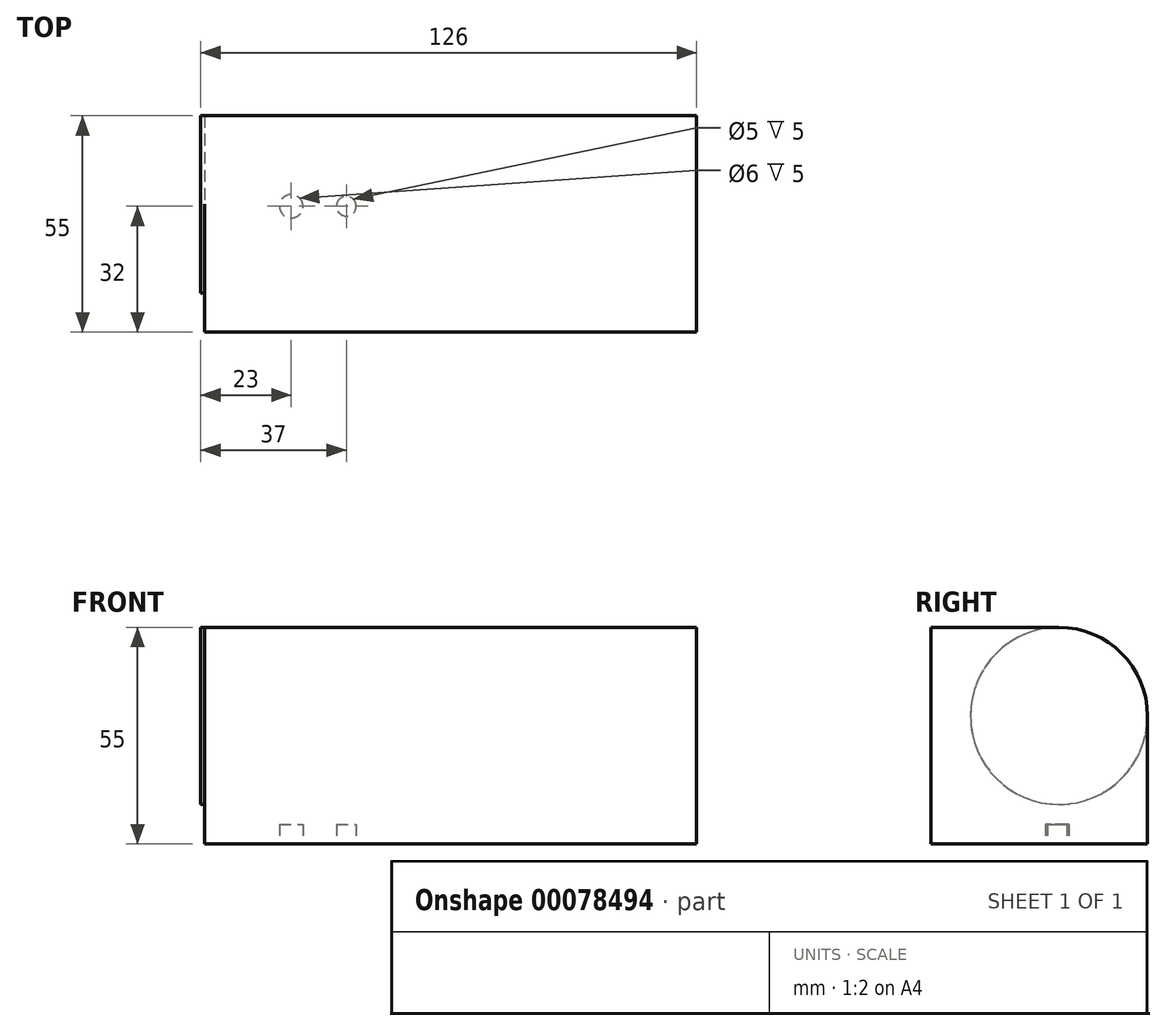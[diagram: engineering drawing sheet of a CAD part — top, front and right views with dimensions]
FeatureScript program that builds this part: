
annotation { "Feature Type Name" : "Feature", "Feature Type Description" : "" }
export const myFeature = defineFeature(function(context is Context, id is Id, definition is map)
    precondition{}
    {
        {
            var Q0;
            Q0=qCreatedBy(makeId("Top.planeOp"),FACE);
            var sketch = newSketch(context, id + "F0", { "sketchPlane" : qUnion([Q0])});
            skLineSegment(sketch, "E0.bottom", {"start": v(62.5, -27.5) * mm, "end": v(-62.5, -27.5) * mm});
            skLineSegment(sketch, "E0.top", {"start": v(62.5, 27.5) * mm, "end": v(-62.5, 27.5) * mm});
            skLineSegment(sketch, "E0.left", {"start": v(62.5, -27.5) * mm, "end": v(62.5, 27.5) * mm});
            skLineSegment(sketch, "E0.right", {"start": v(-62.5, -27.5) * mm, "end": v(-62.5, 27.5) * mm});
            skPoint(sketch, "E0.middle", {"position": v(0, 0) * mm});
            skCircle(sketch, "E1", {"center": v(-40.5, 3.5) * mm, "radius": 3 * mm, "construction": true});
            skSolve(sketch);
        }
        {
            var Q0;
            Q0 = qSketchRegion(id + "F0", true);
            extrude(context, id + "F1", {"entities" : qUnion([Q0]), "depth" : 55 * mm});
        }
        {
            var Q0;
            Q0=makeQuery(id+"F1.opExtrude","CAP_FACE",FACE,{"disambiguationData":[OSD([sQuery(id+"F0.wireOp",EDGE,"E0.bottom"),sQuery(id+"F0.wireOp",EDGE,"E0.top"),sQuery(id+"F0.wireOp",EDGE,"E0.left"),sQuery(id+"F0.wireOp",EDGE,"E0.right")])],"isStart":true});
            var sketch = newSketch(context, id + "F2", { "sketchPlane" : qUnion([Q0])});
            skCircle(sketch, "E2", {"center": v(-40.5, -4.5) * mm, "radius": 3 * mm});
            skCircle(sketch, "E3", {"center": v(-26.5, -4.5) * mm, "radius": 2.5 * mm});
            skSolve(sketch);
        }
        {
            var Q0;
            Q0 = qSketchRegion(id + "F2", true);
            extrude(context, id + "F3", {"entities" : qUnion([Q0]), "operationType" : NewBodyOperationType.REMOVE, "oppositeDirection" : true, "depth" : 5 * mm});
        }
        {
            var Q0;
            Q0=makeQuery(id+"F1.opExtrude","SWEPT_FACE",FACE,{"disambiguationData":[OSD([sQuery(id+"F0.wireOp",EDGE,"E0.right")])]});
            var sketch = newSketch(context, id + "F4", { "sketchPlane" : qUnion([Q0])});
            skCircle(sketch, "E4", {"center": v(-5, 32.5) * mm, "radius": 22.5 * mm});
            skSolve(sketch);
        }
        {
            var Q0;
            Q0 = qSketchRegion(id + "F4", true);
            extrude(context, id + "F5", {"entities" : qUnion([Q0]), "operationType" : NewBodyOperationType.ADD, "depth" : 1 * mm});
        }
        {
            var Q0;
            Q0=makeQuery(id+"F1.opExtrude","CAP_EDGE",EDGE,{"disambiguationData":[OSD([sQuery(id+"F0.wireOp",EDGE,"E0.top")])],"isStart":false});
            fillet(context, id + "F6", {"entities" : qUnion([Q0]), "radius" : 22.5 * mm, "tangentPropagation" : true, "allowEdgeOverflow" : false});
        }
    });
